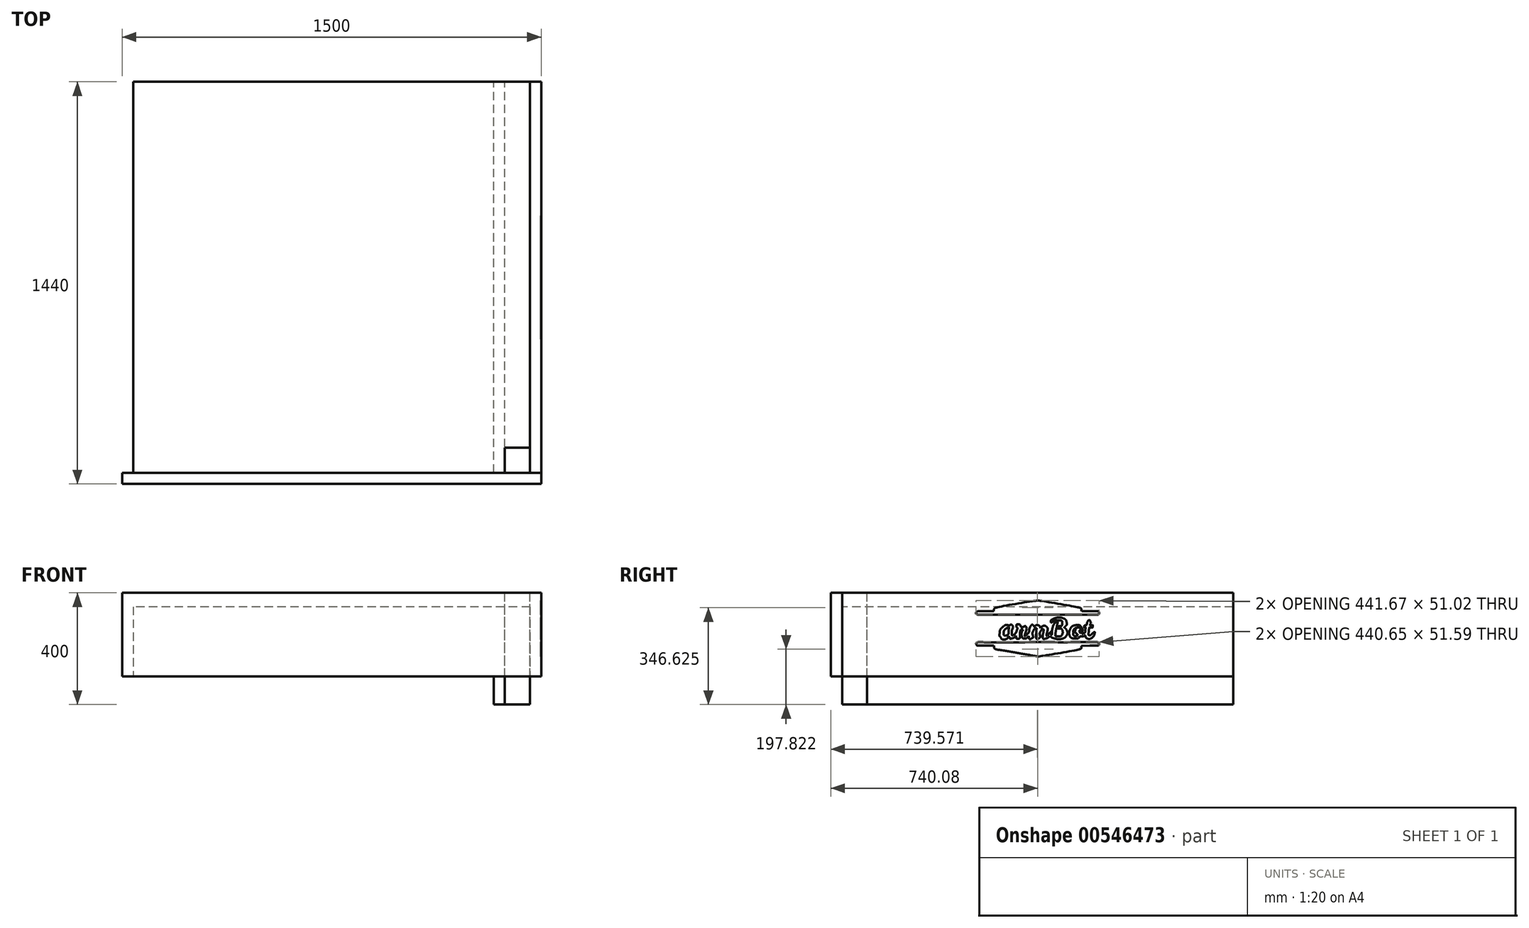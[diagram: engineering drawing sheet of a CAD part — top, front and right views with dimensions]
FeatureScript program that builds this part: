
annotation { "Feature Type Name" : "Feature", "Feature Type Description" : "" }
export const myFeature = defineFeature(function(context is Context, id is Id, definition is map)
    precondition{}
    {
        {
            var Q0;
            Q0=qCreatedBy(makeId("Top.planeOp"),FACE);
            var sketch = newSketch(context, id + "F0", { "sketchPlane" : qUnion([Q0])});
            skLineSegment(sketch, "E0.bottom", {"start": v(710, 700) * mm, "end": v(-710, 700) * mm});
            skLineSegment(sketch, "E0.top", {"start": v(710, -700) * mm, "end": v(-710, -700) * mm});
            skLineSegment(sketch, "E0.left", {"start": v(710, 700) * mm, "end": v(710, -700) * mm});
            skLineSegment(sketch, "E0.right", {"start": v(-710, 700) * mm, "end": v(-710, -700) * mm});
            skPoint(sketch, "E0.middle", {"position": v(0, 0) * mm});
            skSolve(sketch);
        }
        {
            var Q0;
            Q0=qSketchRegion(id+"F0",true);
            extrude(context, id + "F1", {"entities" : qUnion([Q0]), "depth" : 250 * mm});
        }
        {
            var Q0;
            Q0=makeQuery(id+"F1.opExtrude","SWEPT_FACE",FACE,{"disambiguationData":[OSD([sQuery(id+"F0.wireOp",EDGE,"E0.left")])]});
            var sketch = newSketch(context, id + "F2", { "sketchPlane" : qUnion([Q0])});
            skLineSegment(sketch, "E1.bottom", {"start": v(-700, 0) * mm, "end": v(700, 0) * mm});
            skLineSegment(sketch, "E1.top", {"start": v(-700, 300) * mm, "end": v(700, 300) * mm});
            skLineSegment(sketch, "E1.left", {"start": v(-700, 0) * mm, "end": v(-700, 300) * mm});
            skLineSegment(sketch, "E1.right", {"start": v(700, 0) * mm, "end": v(700, 300) * mm});
            skSolve(sketch);
        }
        {
            var Q0;
            Q0=qSketchRegion(id+"F2",true);
            extrude(context, id + "F3", {"entities" : qUnion([Q0]), "depth" : 40 * mm});
        }
        {
            var Q0;
            Q0=makeQuery(id+"F1.opExtrude","SWEPT_FACE",FACE,{"disambiguationData":[OSD([sQuery(id+"F0.wireOp",EDGE,"E0.top")])]});
            var sketch = newSketch(context, id + "F4", { "sketchPlane" : qUnion([Q0])});
            skLineSegment(sketch, "E2.bottom", {"start": v(-750, 300) * mm, "end": v(750, 300) * mm});
            skLineSegment(sketch, "E2.top", {"start": v(-750, 0) * mm, "end": v(750, 0) * mm});
            skLineSegment(sketch, "E2.left", {"start": v(-750, 300) * mm, "end": v(-750, 0) * mm});
            skLineSegment(sketch, "E2.right", {"start": v(750, 300) * mm, "end": v(750, 0) * mm});
            skSolve(sketch);
        }
        {
            var Q0;
            Q0=qSketchRegion(id+"F4",true);
            extrude(context, id + "F5", {"entities" : qUnion([Q0]), "depth" : 40 * mm});
        }
        {
            var Q0;
            Q0=makeQuery(id+"F1.opExtrude","CAP_FACE",FACE,{"disambiguationData":[OSD([sQuery(id+"F0.wireOp",EDGE,"E0.bottom"),sQuery(id+"F0.wireOp",EDGE,"E0.top"),sQuery(id+"F0.wireOp",EDGE,"E0.left"),sQuery(id+"F0.wireOp",EDGE,"E0.right")])],"isStart":false});
            var sketch = newSketch(context, id + "F6", { "sketchPlane" : qUnion([Q0])});
            skFitSpline(sketch, "E3", {"points": [v(-9.76, -247.93) * mm, v(-14.36, -247) * mm, v(-98.7, -232.48) * mm, v(-197.18, -215.67) * mm]});
            skFitSpline(sketch, "E4", {"points": [v(-197.18, -215.67) * mm, v(-303.5, -197.52) * mm, v(-377.79, -184.02) * mm, v(-380.05, -182.43) * mm]});
            skFitSpline(sketch, "E5", {"points": [v(-380.05, -182.43) * mm, v(-386.35, -178.01) * mm, v(-389.22, -172.54) * mm, v(-390.38, -162.7) * mm]});
            skLineSegment(sketch, "E6", {"start": v(-390.38, -162.7) * mm, "end": v(-391.49, -153.38) * mm});
            skLineSegment(sketch, "E7", {"start": v(-391.49, -153.38) * mm, "end": v(-463.29, -153.35) * mm});
            skFitSpline(sketch, "E8", {"points": [v(-463.29, -153.35) * mm, v(-540.74, -153.32) * mm, v(-542.21, -153.15) * mm, v(-546.84, -143.5) * mm]});
            skFitSpline(sketch, "E9", {"points": [v(-546.84, -143.5) * mm, v(-550.32, -136.23) * mm, v(-547.5, -129.03) * mm, v(-539.62, -125.02) * mm]});
            skFitSpline(sketch, "E10", {"points": [v(-539.62, -125.02) * mm, v(-533.58, -121.95) * mm, v(-503.94, -121.77) * mm, v(0.65, -121.77) * mm]});
            skFitSpline(sketch, "E11", {"points": [v(0.65, -121.77) * mm, v(385.66, -121.76) * mm, v(536.18, -122.34) * mm, v(540.43, -123.82) * mm]});
            skFitSpline(sketch, "E12", {"points": [v(540.43, -123.82) * mm, v(543.67, -124.95) * mm, v(547.14, -127.4) * mm, v(548.14, -129.27) * mm]});
            skFitSpline(sketch, "E13", {"points": [v(548.14, -129.27) * mm, v(551.05, -134.7) * mm, v(550.26, -143.3) * mm, v(546.41, -148.06) * mm]});
            skLineSegment(sketch, "E14", {"start": v(546.41, -148.06) * mm, "end": v(542.86, -152.45) * mm});
            skLineSegment(sketch, "E15", {"start": v(542.86, -152.45) * mm, "end": v(467.85, -153.38) * mm});
            skLineSegment(sketch, "E16", {"start": v(467.85, -153.38) * mm, "end": v(392.83, -154.3) * mm});
            skLineSegment(sketch, "E17", {"start": v(392.83, -154.3) * mm, "end": v(392.5, -162.05) * mm});
            skFitSpline(sketch, "E18", {"points": [v(392.5, -162.05) * mm, v(391.99, -173.78) * mm, v(387.68, -180.46) * mm, v(378.46, -183.85) * mm]});
            skFitSpline(sketch, "E19", {"points": [v(378.46, -183.85) * mm, v(371.97, -186.24) * mm, v(2.57, -250.58) * mm, v(-0.47, -249.85) * mm]});
            skFitSpline(sketch, "E20", {"points": [v(-0.47, -249.85) * mm, v(-0.98, -249.73) * mm, v(-5.16, -248.87) * mm, v(-9.76, -247.93) * mm]});
            skLineSegment(sketch, "E21", {"start": v(-9.76, -247.93) * mm, "end": v(-9.76, -247.93) * mm});
            skFitSpline(sketch, "E22", {"points": [v(163.18, -91.34) * mm, v(144.56, -86.99) * mm, v(127.82, -80.58) * mm, v(118.25, -74.15) * mm]});
            skLineSegment(sketch, "E23", {"start": v(118.25, -74.15) * mm, "end": v(108.82, -67.8) * mm});
            skLineSegment(sketch, "E24", {"start": v(108.82, -67.8) * mm, "end": v(101.7, -74.22) * mm});
            skFitSpline(sketch, "E25", {"points": [v(101.7, -74.22) * mm, v(92.92, -82.15) * mm, v(86.06, -85.78) * mm, v(75.22, -88.2) * mm]});
            skFitSpline(sketch, "E26", {"points": [v(75.22, -88.2) * mm, v(52.86, -93.22) * mm, v(44.33, -75.76) * mm, v(50.52, -37.64) * mm]});
            skFitSpline(sketch, "E27", {"points": [v(50.52, -37.64) * mm, v(54.63, -12.34) * mm, v(54.44, -8.7) * mm, v(48.9, -6.17) * mm]});
            skFitSpline(sketch, "E28", {"points": [v(48.9, -6.17) * mm, v(42.7, -3.35) * mm, v(36.64, -7.44) * mm, v(29.87, -18.99) * mm]});
            skFitSpline(sketch, "E29", {"points": [v(29.87, -18.99) * mm, v(21.01, -34.1) * mm, v(18.43, -44.15) * mm, v(20.53, -55.3) * mm]});
            skFitSpline(sketch, "E30", {"points": [v(20.53, -55.3) * mm, v(21.54, -60.66) * mm, v(22.46, -68.35) * mm, v(22.57, -72.38) * mm]});
            skFitSpline(sketch, "E31", {"points": [v(22.57, -72.38) * mm, v(22.76, -78.97) * mm, v(22, -80.26) * mm, v(14.95, -85.23) * mm]});
            skFitSpline(sketch, "E32", {"points": [v(14.95, -85.23) * mm, v(4.39, -92.68) * mm, v(-7.54, -93.24) * mm, v(-11.04, -86.43) * mm]});
            skFitSpline(sketch, "E33", {"points": [v(-11.04, -86.43) * mm, v(-13.95, -80.76) * mm, v(-14.16, -56.28) * mm, v(-11.54, -26.93) * mm]});
            skFitSpline(sketch, "E34", {"points": [v(-11.54, -26.93) * mm, v(-9.2, -0.66) * mm, v(-9.84, 2.83) * mm, v(-17.07, 2.83) * mm]});
            skFitSpline(sketch, "E35", {"points": [v(-17.07, 2.83) * mm, v(-23.9, 2.83) * mm, v(-30.46, -4.7) * mm, v(-38.87, -22.23) * mm]});
            skFitSpline(sketch, "E36", {"points": [v(-38.87, -22.23) * mm, v(-45.93, -36.93) * mm, v(-46.62, -45.33) * mm, v(-42.27, -63.77) * mm]});
            skFitSpline(sketch, "E37", {"points": [v(-42.27, -63.77) * mm, v(-38.91, -78.01) * mm, v(-39.9, -80.3) * mm, v(-52.19, -87) * mm]});
            skFitSpline(sketch, "E38", {"points": [v(-52.19, -87) * mm, v(-68.26, -95.75) * mm, v(-75.2, -92.86) * mm, v(-77.56, -76.43) * mm]});
            skLineSegment(sketch, "E39", {"start": v(-77.56, -76.43) * mm, "end": v(-78.86, -67.36) * mm});
            skLineSegment(sketch, "E40", {"start": v(-78.86, -67.36) * mm, "end": v(-86.62, -74.83) * mm});
            skFitSpline(sketch, "E41", {"points": [v(-86.62, -74.83) * mm, v(-97.05, -84.9) * mm, v(-104.92, -88.54) * mm, v(-116.78, -88.82) * mm]});
            skFitSpline(sketch, "E42", {"points": [v(-116.78, -88.82) * mm, v(-128.34, -89.1) * mm, v(-132.94, -86) * mm, v(-138.3, -74.35) * mm]});
            skFitSpline(sketch, "E43", {"points": [v(-138.3, -74.35) * mm, v(-144.12, -61.65) * mm, v(-141.58, -31.54) * mm, v(-133.32, -15.58) * mm]});
            skLineSegment(sketch, "E44", {"start": v(-133.32, -15.58) * mm, "end": v(-130.44, -10) * mm});
            skLineSegment(sketch, "E45", {"start": v(-130.44, -10) * mm, "end": v(-141.2, -10.56) * mm});
            skLineSegment(sketch, "E46", {"start": v(-141.2, -10.56) * mm, "end": v(-151.94, -11.12) * mm});
            skLineSegment(sketch, "E47", {"start": v(-151.94, -11.12) * mm, "end": v(-155.34, -25.07) * mm});
            skFitSpline(sketch, "E48", {"points": [v(-155.34, -25.07) * mm, v(-157.97, -35.9) * mm, v(-158.52, -43.56) * mm, v(-157.8, -59.34) * mm]});
            skFitSpline(sketch, "E49", {"points": [v(-157.8, -59.34) * mm, v(-157.29, -70.85) * mm, v(-157.67, -81.12) * mm, v(-158.7, -83.03) * mm]});
            skFitSpline(sketch, "E50", {"points": [v(-158.7, -83.03) * mm, v(-161.25, -87.81) * mm, v(-170.24, -92.01) * mm, v(-177.92, -92.01) * mm]});
            skFitSpline(sketch, "E51", {"points": [v(-177.92, -92.01) * mm, v(-186.08, -92.01) * mm, v(-189.42, -87.45) * mm, v(-191.2, -73.87) * mm]});
            skLineSegment(sketch, "E52", {"start": v(-191.2, -73.87) * mm, "end": v(-192.48, -64.09) * mm});
            skLineSegment(sketch, "E53", {"start": v(-192.48, -64.09) * mm, "end": v(-200.42, -71.4) * mm});
            skFitSpline(sketch, "E54", {"points": [v(-200.42, -71.4) * mm, v(-209.89, -80.13) * mm, v(-220.17, -85.65) * mm, v(-231.87, -88.27) * mm]});
            skFitSpline(sketch, "E55", {"points": [v(-231.87, -88.27) * mm, v(-243.7, -90.92) * mm, v(-250.08, -87.49) * mm, v(-254.4, -76.16) * mm]});
            skLineSegment(sketch, "E56", {"start": v(-254.4, -76.16) * mm, "end": v(-257.65, -67.68) * mm});
            skLineSegment(sketch, "E57", {"start": v(-257.65, -67.68) * mm, "end": v(-262.94, -74.1) * mm});
            skFitSpline(sketch, "E58", {"points": [v(-262.94, -74.1) * mm, v(-279.38, -94.04) * mm, v(-316.37, -95.84) * mm, v(-331.85, -77.45) * mm]});
            skFitSpline(sketch, "E59", {"points": [v(-331.85, -77.45) * mm, v(-339.17, -68.75) * mm, v(-341.42, -59.86) * mm, v(-340.14, -44.75) * mm]});
            skFitSpline(sketch, "E60", {"points": [v(-340.14, -44.75) * mm, v(-338.13, -20.94) * mm, v(-329.14, -1.86) * mm, v(-313.1, 12.61) * mm]});
            skFitSpline(sketch, "E61", {"points": [v(-313.1, 12.61) * mm, v(-297.94, 26.32) * mm, v(-276.95, 32.69) * mm, v(-259.7, 28.82) * mm]});
            skFitSpline(sketch, "E62", {"points": [v(-259.7, 28.82) * mm, v(-252.55, 27.22) * mm, v(-250.45, 27.38) * mm, v(-247.85, 29.73) * mm]});
            skFitSpline(sketch, "E63", {"points": [v(-247.85, 29.73) * mm, v(-240.93, 36) * mm, v(-226.99, 30.32) * mm, v(-220.73, 18.7) * mm]});
            skLineSegment(sketch, "E64", {"start": v(-220.73, 18.7) * mm, "end": v(-217.21, 12.17) * mm});
            skLineSegment(sketch, "E65", {"start": v(-217.21, 12.17) * mm, "end": v(-223.2, 0.02) * mm});
            skFitSpline(sketch, "E66", {"points": [v(-223.2, 0.02) * mm, v(-228.92, -11.58) * mm, v(-229.19, -13.1) * mm, v(-229.16, -33.94) * mm]});
            skFitSpline(sketch, "E67", {"points": [v(-229.16, -33.94) * mm, v(-229.13, -57.9) * mm, v(-228.1, -61.48) * mm, v(-221.81, -59.49) * mm]});
            skFitSpline(sketch, "E68", {"points": [v(-221.81, -59.49) * mm, v(-215.07, -57.35) * mm, v(-188.28, -30.28) * mm, v(-188.28, -25.6) * mm]});
            skFitSpline(sketch, "E69", {"points": [v(-188.28, -25.6) * mm, v(-188.28, -23.36) * mm, v(-186.22, -15.85) * mm, v(-183.7, -8.92) * mm]});
            skFitSpline(sketch, "E70", {"points": [v(-183.7, -8.92) * mm, v(-179.26, 3.33) * mm, v(-179.23, 3.78) * mm, v(-182.54, 7.44) * mm]});
            skFitSpline(sketch, "E71", {"points": [v(-182.54, 7.44) * mm, v(-188.48, 13.98) * mm, v(-190.53, 19.67) * mm, v(-189.3, 26.21) * mm]});
            skFitSpline(sketch, "E72", {"points": [v(-189.3, 26.21) * mm, v(-187.82, 34.15) * mm, v(-182.12, 38.16) * mm, v(-172.31, 38.16) * mm]});
            skFitSpline(sketch, "E73", {"points": [v(-172.31, 38.16) * mm, v(-163.16, 38.16) * mm, v(-156.23, 32.34) * mm, v(-150.73, 20.03) * mm]});
            skFitSpline(sketch, "E74", {"points": [v(-150.73, 20.03) * mm, v(-147.7, 13.24) * mm, v(-146.4, 12.12) * mm, v(-141.55, 12.12) * mm]});
            skFitSpline(sketch, "E75", {"points": [v(-141.55, 12.12) * mm, v(-138.45, 12.12) * mm, v(-130.4, 14.33) * mm, v(-123.66, 17.03) * mm]});
            skFitSpline(sketch, "E76", {"points": [v(-123.66, 17.03) * mm, v(-109.3, 22.78) * mm, v(-107.41, 22.17) * mm, v(-101.2, 9.8) * mm]});
            skLineSegment(sketch, "E77", {"start": v(-101.2, 9.8) * mm, "end": v(-96.87, 1.18) * mm});
            skLineSegment(sketch, "E78", {"start": v(-96.87, 1.18) * mm, "end": v(-104.6, -26.95) * mm});
            skFitSpline(sketch, "E79", {"points": [v(-104.6, -26.95) * mm, v(-115.26, -65.72) * mm, v(-113.52, -68.38) * mm, v(-91.12, -47.46) * mm]});
            skLineSegment(sketch, "E80", {"start": v(-91.12, -47.46) * mm, "end": v(-77.26, -34.51) * mm});
            skLineSegment(sketch, "E81", {"start": v(-77.26, -34.51) * mm, "end": v(-76.15, -22.7) * mm});
            skFitSpline(sketch, "E82", {"points": [v(-76.15, -22.7) * mm, v(-74.76, -7.77) * mm, v(-68.68, 10.87) * mm, v(-61.04, 23.61) * mm]});
            skFitSpline(sketch, "E83", {"points": [v(-61.04, 23.61) * mm, v(-56.21, 31.68) * mm, v(-54.07, 33.61) * mm, v(-49.45, 34.07) * mm]});
            skFitSpline(sketch, "E84", {"points": [v(-49.45, 34.07) * mm, v(-44.95, 34.52) * mm, v(-42.63, 33.32) * mm, v(-38.15, 28.2) * mm]});
            skFitSpline(sketch, "E85", {"points": [v(-38.15, 28.2) * mm, v(-35.04, 24.67) * mm, v(-32.16, 20.74) * mm, v(-31.73, 19.46) * mm]});
            skFitSpline(sketch, "E86", {"points": [v(-31.73, 19.46) * mm, v(-31.21, 17.9) * mm, v(-28.37, 19.02) * mm, v(-23, 22.9) * mm]});
            skFitSpline(sketch, "E87", {"points": [v(-23, 22.9) * mm, v(-11.96, 30.9) * mm, v(-1.17, 32.3) * mm, v(9.54, 27.1) * mm]});
            skFitSpline(sketch, "E88", {"points": [v(9.54, 27.1) * mm, v(18.23, 22.9) * mm, v(22.7, 17.7) * mm, v(24.79, 9.4) * mm]});
            skLineSegment(sketch, "E89", {"start": v(24.79, 9.4) * mm, "end": v(26.04, 4.44) * mm});
            skLineSegment(sketch, "E90", {"start": v(26.04, 4.44) * mm, "end": v(30.92, 9.1) * mm});
            skFitSpline(sketch, "E91", {"points": [v(30.92, 9.1) * mm, v(43.6, 21.22) * mm, v(66.06, 25.1) * mm, v(77.8, 17.18) * mm]});
            skFitSpline(sketch, "E92", {"points": [v(77.8, 17.18) * mm, v(81.26, 14.85) * mm, v(85.14, 10.88) * mm, v(86.42, 8.35) * mm]});
            skFitSpline(sketch, "E93", {"points": [v(86.42, 8.35) * mm, v(90.04, 1.18) * mm, v(89.21, -14.95) * mm, v(84.14, -35.88) * mm]});
            skFitSpline(sketch, "E94", {"points": [v(84.14, -35.88) * mm, v(81.59, -46.43) * mm, v(79.5, -56.26) * mm, v(79.5, -57.73) * mm]});
            skFitSpline(sketch, "E95", {"points": [v(79.5, -57.73) * mm, v(79.5, -63.6) * mm, v(86.26, -59.69) * mm, v(100.97, -45.33) * mm]});
            skFitSpline(sketch, "E96", {"points": [v(100.97, -45.33) * mm, v(110.63, -35.9) * mm, v(117.25, -30.77) * mm, v(118.65, -31.64) * mm]});
            skFitSpline(sketch, "E97", {"points": [v(118.65, -31.64) * mm, v(120.17, -32.58) * mm, v(120.56, -36.5) * mm, v(119.89, -43.92) * mm]});
            skFitSpline(sketch, "E98", {"points": [v(119.89, -43.92) * mm, v(118.95, -54.29) * mm, v(119.1, -54.82) * mm, v(123.1, -54.82) * mm]});
            skFitSpline(sketch, "E99", {"points": [v(123.1, -54.82) * mm, v(127.02, -54.82) * mm, v(127.36, -53.84) * mm, v(128.4, -39.48) * mm]});
            skFitSpline(sketch, "E100", {"points": [v(128.4, -39.48) * mm, v(130.72, -7.09) * mm, v(148.03, 43.77) * mm, v(160.6, 55.09) * mm]});
            skFitSpline(sketch, "E101", {"points": [v(160.6, 55.09) * mm, v(178.01, 70.78) * mm, v(179.9, 58.14) * mm, v(168.42, 2.83) * mm]});
            skFitSpline(sketch, "E102", {"points": [v(168.42, 2.83) * mm, v(163.73, -19.8) * mm, v(158.67, -63.5) * mm, v(160.5, -65.68) * mm]});
            skFitSpline(sketch, "E103", {"points": [v(160.5, -65.68) * mm, v(161.76, -67.18) * mm, v(175.96, -69.61) * mm, v(183.63, -69.64) * mm]});
            skFitSpline(sketch, "E104", {"points": [v(183.63, -69.64) * mm, v(200.98, -69.71) * mm, v(215.69, -61.64) * mm, v(220.83, -49.22) * mm]});
            skFitSpline(sketch, "E105", {"points": [v(220.83, -49.22) * mm, v(224.51, -40.34) * mm, v(222.43, -16.02) * mm, v(217.28, -7.68) * mm]});
            skFitSpline(sketch, "E106", {"points": [v(217.28, -7.68) * mm, v(213.13, -0.96) * mm, v(212.95, -0.9) * mm, v(200.63, -0.9) * mm]});
            skFitSpline(sketch, "E107", {"points": [v(200.63, -0.9) * mm, v(187.27, -0.9) * mm, v(181.1, 1.8) * mm, v(179.39, 8.35) * mm]});
            skFitSpline(sketch, "E108", {"points": [v(179.39, 8.35) * mm, v(178.82, 10.5) * mm, v(179.82, 13.89) * mm, v(181.7, 16.2) * mm]});
            skFitSpline(sketch, "E109", {"points": [v(181.7, 16.2) * mm, v(184.4, 19.56) * mm, v(187.56, 20.46) * mm, v(199.63, 21.31) * mm]});
            skFitSpline(sketch, "E110", {"points": [v(199.63, 21.31) * mm, v(213.63, 22.3) * mm, v(214.4, 22.6) * mm, v(217.02, 27.93) * mm]});
            skFitSpline(sketch, "E111", {"points": [v(217.02, 27.93) * mm, v(218.53, 31) * mm, v(219.77, 38.53) * mm, v(219.78, 44.67) * mm]});
            skFitSpline(sketch, "E112", {"points": [v(219.78, 44.67) * mm, v(219.8, 64.17) * mm, v(211.17, 71.67) * mm, v(187.07, 73.1) * mm]});
            skFitSpline(sketch, "E113", {"points": [v(187.07, 73.1) * mm, v(170.05, 74.11) * mm, v(157.7, 71.45) * mm, v(139.99, 62.97) * mm]});
            skFitSpline(sketch, "E114", {"points": [v(139.99, 62.97) * mm, v(124.82, 55.7) * mm, v(118.55, 54.98) * mm, v(118.55, 60.51) * mm]});
            skFitSpline(sketch, "E115", {"points": [v(118.55, 60.51) * mm, v(118.55, 70.5) * mm, v(143.11, 88.38) * mm, v(165.9, 94.95) * mm]});
            skFitSpline(sketch, "E116", {"points": [v(165.9, 94.95) * mm, v(181.16, 99.36) * mm, v(211.58, 97.92) * mm, v(227.33, 92.04) * mm]});
            skFitSpline(sketch, "E117", {"points": [v(227.33, 92.04) * mm, v(241.91, 86.6) * mm, v(254.67, 73.92) * mm, v(257.71, 61.83) * mm]});
            skFitSpline(sketch, "E118", {"points": [v(257.71, 61.83) * mm, v(262.48, 42.9) * mm, v(259.33, 31.38) * mm, v(245.79, 18.17) * mm]});
            skFitSpline(sketch, "E119", {"points": [v(245.79, 18.17) * mm, v(240.28, 12.8) * mm, v(236.48, 8.4) * mm, v(237.34, 8.4) * mm]});
            skFitSpline(sketch, "E120", {"points": [v(237.34, 8.4) * mm, v(241.01, 8.4) * mm, v(256.17, -7.19) * mm, v(259.81, -14.71) * mm]});
            skFitSpline(sketch, "E121", {"points": [v(259.81, -14.71) * mm, v(265.46, -26.39) * mm, v(265.68, -49.04) * mm, v(260.25, -59.68) * mm]});
            skFitSpline(sketch, "E122", {"points": [v(260.25, -59.68) * mm, v(254.38, -71.16) * mm, v(239.5, -83.55) * mm, v(225.92, -88.28) * mm]});
            skFitSpline(sketch, "E123", {"points": [v(225.92, -88.28) * mm, v(211.44, -93.33) * mm, v(178.53, -94.93) * mm, v(163.18, -91.34) * mm]});
            skFitSpline(sketch, "E124", {"points": [v(-281.84, -62.14) * mm, v(-267.85, -56.85) * mm, v(-259.05, -41.8) * mm, v(-258.98, -23.08) * mm]});
            skFitSpline(sketch, "E125", {"points": [v(-258.98, -23.08) * mm, v(-258.96, -16.37) * mm, v(-258.05, -6.04) * mm, v(-256.95, -0.12) * mm]});
            skFitSpline(sketch, "E126", {"points": [v(-256.95, -0.12) * mm, v(-255.86, 5.8) * mm, v(-255.42, 11.09) * mm, v(-255.98, 11.64) * mm]});
            skFitSpline(sketch, "E127", {"points": [v(-255.98, 11.64) * mm, v(-257.93, 13.6) * mm, v(-273.99, 6.15) * mm, v(-282.7, -0.75) * mm]});
            skFitSpline(sketch, "E128", {"points": [v(-282.7, -0.75) * mm, v(-295.24, -10.66) * mm, v(-302.1, -24.16) * mm, v(-303.18, -41.06) * mm]});
            skFitSpline(sketch, "E129", {"points": [v(-303.18, -41.06) * mm, v(-303.98, -53.62) * mm, v(-303.72, -54.84) * mm, v(-299.24, -59.32) * mm]});
            skFitSpline(sketch, "E130", {"points": [v(-299.24, -59.32) * mm, v(-294.03, -64.53) * mm, v(-289.93, -65.2) * mm, v(-281.84, -62.14) * mm]});
            skFitSpline(sketch, "E131", {"points": [v(-459.3, -89.94) * mm, v(-464.48, -84.62) * mm, v(-460.7, -35.47) * mm, v(-453.32, -12.23) * mm]});
            skFitSpline(sketch, "E132", {"points": [v(-453.32, -12.23) * mm, v(-452.15, -8.52) * mm, v(-452.73, -8.33) * mm, v(-465.23, -8.33) * mm]});
            skFitSpline(sketch, "E133", {"points": [v(-465.23, -8.33) * mm, v(-476.68, -8.33) * mm, v(-478.37, -7.9) * mm, v(-478.37, -4.96) * mm]});
            skFitSpline(sketch, "E134", {"points": [v(-478.37, -4.96) * mm, v(-478.37, 0.26) * mm, v(-468.99, 8.03) * mm, v(-457.1, 12.63) * mm]});
            skLineSegment(sketch, "E135", {"start": v(-457.1, 12.63) * mm, "end": v(-446.32, 16.8) * mm});
            skLineSegment(sketch, "E136", {"start": v(-446.32, 16.8) * mm, "end": v(-438.43, 39.1) * mm});
            skFitSpline(sketch, "E137", {"points": [v(-438.43, 39.1) * mm, v(-434.08, 51.37) * mm, v(-429.87, 62.96) * mm, v(-429.07, 64.87) * mm]});
            skFitSpline(sketch, "E138", {"points": [v(-429.07, 64.87) * mm, v(-427.72, 68.05) * mm, v(-428.28, 68.22) * mm, v(-435.78, 67) * mm]});
            skFitSpline(sketch, "E139", {"points": [v(-435.78, 67) * mm, v(-447.95, 65.04) * mm, v(-458.5, 59.86) * mm, v(-467.75, 51.34) * mm]});
            skFitSpline(sketch, "E140", {"points": [v(-467.75, 51.34) * mm, v(-479.66, 40.36) * mm, v(-483.95, 41.51) * mm, v(-483.95, 55.7) * mm]});
            skFitSpline(sketch, "E141", {"points": [v(-483.95, 55.7) * mm, v(-483.95, 68.83) * mm, v(-467.73, 83.32) * mm, v(-445.28, 90.26) * mm]});
            skFitSpline(sketch, "E142", {"points": [v(-445.28, 90.26) * mm, v(-427.1, 95.87) * mm, v(-406.05, 97.33) * mm, v(-358.74, 96.25) * mm]});
            skFitSpline(sketch, "E143", {"points": [v(-358.74, 96.25) * mm, v(-311.18, 95.17) * mm, v(-311.95, 95.43) * mm, v(-317.58, 82.22) * mm]});
            skFitSpline(sketch, "E144", {"points": [v(-317.58, 82.22) * mm, v(-323.64, 68.03) * mm, v(-324, 67.91) * mm, v(-360.96, 67.88) * mm]});
            skLineSegment(sketch, "E145", {"start": v(-360.96, 67.88) * mm, "end": v(-393.76, 67.85) * mm});
            skLineSegment(sketch, "E146", {"start": v(-393.76, 67.85) * mm, "end": v(-398.66, 47.9) * mm});
            skFitSpline(sketch, "E147", {"points": [v(-398.66, 47.9) * mm, v(-401.36, 36.91) * mm, v(-403.87, 26.67) * mm, v(-404.24, 25.14) * mm]});
            skFitSpline(sketch, "E148", {"points": [v(-404.24, 25.14) * mm, v(-404.8, 22.8) * mm, v(-401.23, 22.27) * mm, v(-381.74, 21.83) * mm]});
            skFitSpline(sketch, "E149", {"points": [v(-381.74, 21.83) * mm, v(-367.15, 21.5) * mm, v(-358.1, 20.53) * mm, v(-357.28, 19.21) * mm]});
            skFitSpline(sketch, "E150", {"points": [v(-357.28, 19.21) * mm, v(-355.76, 16.75) * mm, v(-359.89, 2.02) * mm, v(-363.24, -2.01) * mm]});
            skFitSpline(sketch, "E151", {"points": [v(-363.24, -2.01) * mm, v(-365.2, -4.38) * mm, v(-369.3, -4.62) * mm, v(-389.06, -3.54) * mm]});
            skLineSegment(sketch, "E152", {"start": v(-389.06, -3.54) * mm, "end": v(-412.56, -2.27) * mm});
            skLineSegment(sketch, "E153", {"start": v(-412.56, -2.27) * mm, "end": v(-416.52, -18.78) * mm});
            skFitSpline(sketch, "E154", {"points": [v(-416.52, -18.78) * mm, v(-421.04, -37.64) * mm, v(-423.77, -53.93) * mm, v(-425.45, -72.08) * mm]});
            skFitSpline(sketch, "E155", {"points": [v(-425.45, -72.08) * mm, v(-426.44, -82.86) * mm, v(-427.3, -85.14) * mm, v(-431.33, -87.78) * mm]});
            skFitSpline(sketch, "E156", {"points": [v(-431.33, -87.78) * mm, v(-437.41, -91.77) * mm, v(-456.13, -93.2) * mm, v(-459.3, -89.94) * mm]});
            skFitSpline(sketch, "E157", {"points": [v(317.5, -88.5) * mm, v(302.9, -83.79) * mm, v(289.51, -71.3) * mm, v(285.81, -58.96) * mm]});
            skFitSpline(sketch, "E158", {"points": [v(285.81, -58.96) * mm, v(282.17, -46.8) * mm, v(284.25, -22.14) * mm, v(289.96, -9.87) * mm]});
            skFitSpline(sketch, "E159", {"points": [v(289.96, -9.87) * mm, v(299.26, 10.12) * mm, v(316.09, 24.32) * mm, v(335.9, 28.9) * mm]});
            skFitSpline(sketch, "E160", {"points": [v(335.9, 28.9) * mm, v(354.07, 33.1) * mm, v(378.44, 28.13) * mm, v(386.33, 18.63) * mm]});
            skFitSpline(sketch, "E161", {"points": [v(386.33, 18.63) * mm, v(390.02, 14.18) * mm, v(386.8, 12.82) * mm, v(369.86, 11.65) * mm]});
            skFitSpline(sketch, "E162", {"points": [v(369.86, 11.65) * mm, v(362, 11.12) * mm, v(352.6, 9.43) * mm, v(348.96, 7.91) * mm]});
            skFitSpline(sketch, "E163", {"points": [v(348.96, 7.91) * mm, v(331.95, 0.8) * mm, v(320.77, -16.17) * mm, v(320.52, -35.3) * mm]});
            skFitSpline(sketch, "E164", {"points": [v(320.52, -35.3) * mm, v(320.22, -57.93) * mm, v(334.52, -68.41) * mm, v(357.15, -62.13) * mm]});
            skLineSegment(sketch, "E165", {"start": v(357.15, -62.13) * mm, "end": v(364.23, -60.16) * mm});
            skLineSegment(sketch, "E166", {"start": v(364.23, -60.16) * mm, "end": v(357.84, -53.09) * mm});
            skFitSpline(sketch, "E167", {"points": [v(357.84, -53.09) * mm, v(336.45, -29.41) * mm, v(349.03, 6.55) * mm, v(378.7, 6.55) * mm]});
            skFitSpline(sketch, "E168", {"points": [v(378.7, 6.55) * mm, v(389.23, 6.55) * mm, v(395.06, 3.8) * mm, v(399.43, -3.17) * mm]});
            skFitSpline(sketch, "E169", {"points": [v(399.43, -3.17) * mm, v(402.65, -8.3) * mm, v(403.12, -11.47) * mm, v(402.44, -23.2) * mm]});
            skFitSpline(sketch, "E170", {"points": [v(402.44, -23.2) * mm, v(402, -30.88) * mm, v(401.02, -39.04) * mm, v(400.27, -41.34) * mm]});
            skFitSpline(sketch, "E171", {"points": [v(400.27, -41.34) * mm, v(398.58, -46.51) * mm, v(402.33, -46.92) * mm, v(411.06, -42.52) * mm]});
            skFitSpline(sketch, "E172", {"points": [v(411.06, -42.52) * mm, v(421.31, -37.33) * mm, v(425.37, -32.45) * mm, v(425.44, -25.2) * mm]});
            skFitSpline(sketch, "E173", {"points": [v(425.44, -25.2) * mm, v(425.48, -21.55) * mm, v(426.6, -12.92) * mm, v(427.94, -6.02) * mm]});
            skFitSpline(sketch, "E174", {"points": [v(427.94, -6.02) * mm, v(429.27, 0.87) * mm, v(429.94, 6.94) * mm, v(429.42, 7.46) * mm]});
            skFitSpline(sketch, "E175", {"points": [v(429.42, 7.46) * mm, v(428.9, 7.98) * mm, v(425.6, 8.4) * mm, v(422.07, 8.4) * mm]});
            skFitSpline(sketch, "E176", {"points": [v(422.07, 8.4) * mm, v(415.71, 8.4) * mm, v(415.67, 8.46) * mm, v(416.93, 15.14) * mm]});
            skFitSpline(sketch, "E177", {"points": [v(416.93, 15.14) * mm, v(418.93, 25.81) * mm, v(421.68, 28.86) * mm, v(429.3, 28.86) * mm]});
            skFitSpline(sketch, "E178", {"points": [v(429.3, 28.86) * mm, v(435.8, 28.86) * mm, v(436.17, 29.23) * mm, v(439.97, 39.55) * mm]});
            skFitSpline(sketch, "E179", {"points": [v(439.97, 39.55) * mm, v(450.84, 69.05) * mm, v(465.01, 75.94) * mm, v(473.83, 56) * mm]});
            skLineSegment(sketch, "E180", {"start": v(473.83, 56) * mm, "end": v(477.45, 47.84) * mm});
            skLineSegment(sketch, "E181", {"start": v(477.45, 47.84) * mm, "end": v(472.82, 39.75) * mm});
            skFitSpline(sketch, "E182", {"points": [v(472.82, 39.75) * mm, v(470.27, 35.3) * mm, v(468.18, 31.02) * mm, v(468.17, 30.25) * mm]});
            skFitSpline(sketch, "E183", {"points": [v(468.17, 30.25) * mm, v(468.15, 29.49) * mm, v(474, 28.86) * mm, v(481.16, 28.86) * mm]});
            skFitSpline(sketch, "E184", {"points": [v(481.16, 28.86) * mm, v(493.59, 28.86) * mm, v(494.18, 28.66) * mm, v(494.18, 24.49) * mm]});
            skFitSpline(sketch, "E185", {"points": [v(494.18, 24.49) * mm, v(494.18, 22.08) * mm, v(493.26, 17.48) * mm, v(492.14, 14.26) * mm]});
            skFitSpline(sketch, "E186", {"points": [v(492.14, 14.26) * mm, v(490.1, 8.41) * mm, v(490.07, 8.4) * mm, v(476.53, 8.4) * mm]});
            skFitSpline(sketch, "E187", {"points": [v(476.53, 8.4) * mm, v(466.58, 8.4) * mm, v(462.7, 7.7) * mm, v(461.96, 5.79) * mm]});
            skFitSpline(sketch, "E188", {"points": [v(461.96, 5.79) * mm, v(461.4, 4.35) * mm, v(459.93, -6.74) * mm, v(458.69, -18.85) * mm]});
            skFitSpline(sketch, "E189", {"points": [v(458.69, -18.85) * mm, v(456.19, -43.13) * mm, v(457.42, -58.1) * mm, v(462.05, -59.89) * mm]});
            skFitSpline(sketch, "E190", {"points": [v(462.05, -59.89) * mm, v(466.54, -61.6) * mm, v(480.7, -53.25) * mm, v(493.44, -41.34) * mm]});
            skFitSpline(sketch, "E191", {"points": [v(493.44, -41.34) * mm, v(499.73, -35.46) * mm, v(505.73, -30.65) * mm, v(506.77, -30.65) * mm]});
            skFitSpline(sketch, "E192", {"points": [v(506.77, -30.65) * mm, v(510.1, -30.65) * mm, v(511.02, -39.58) * mm, v(508.46, -47.01) * mm]});
            skFitSpline(sketch, "E193", {"points": [v(508.46, -47.01) * mm, v(500.27, -70.78) * mm, v(464.23, -93.67) * mm, v(443.63, -88.18) * mm]});
            skFitSpline(sketch, "E194", {"points": [v(443.63, -88.18) * mm, v(436.32, -86.23) * mm, v(430.49, -78.96) * mm, v(428.05, -68.77) * mm]});
            skFitSpline(sketch, "E195", {"points": [v(428.05, -68.77) * mm, v(426, -60.18) * mm, v(425.55, -59.99) * mm, v(418.25, -64.52) * mm]});
            skFitSpline(sketch, "E196", {"points": [v(418.25, -64.52) * mm, v(412.67, -68) * mm, v(408.97, -68.73) * mm, v(397.88, -68.57) * mm]});
            skFitSpline(sketch, "E197", {"points": [v(397.88, -68.57) * mm, v(384.98, -68.4) * mm, v(384.01, -68.68) * mm, v(377.5, -74.64) * mm]});
            skFitSpline(sketch, "E198", {"points": [v(377.5, -74.64) * mm, v(365.8, -85.37) * mm, v(355.8, -89.15) * mm, v(337.98, -89.6) * mm]});
            skFitSpline(sketch, "E199", {"points": [v(337.98, -89.6) * mm, v(329.28, -89.82) * mm, v(320.07, -89.33) * mm, v(317.5, -88.5) * mm]});
            skFitSpline(sketch, "E200", {"points": [v(385.7, -25.43) * mm, v(386.64, -17.46) * mm, v(386.3, -15.64) * mm, v(383.66, -14.63) * mm]});
            skFitSpline(sketch, "E201", {"points": [v(383.66, -14.63) * mm, v(379.08, -12.87) * mm, v(376.38, -16.52) * mm, v(376.67, -24.09) * mm]});
            skFitSpline(sketch, "E202", {"points": [v(376.67, -24.09) * mm, v(376.97, -32.15) * mm, v(380.4, -39.18) * mm, v(382.83, -36.75) * mm]});
            skFitSpline(sketch, "E203", {"points": [v(382.83, -36.75) * mm, v(383.78, -35.8) * mm, v(385.07, -30.7) * mm, v(385.7, -25.43) * mm]});
            skFitSpline(sketch, "E204", {"points": [v(-539.73, 126.1) * mm, v(-551.06, 131.84) * mm, v(-551, 146.27) * mm, v(-539.62, 152.05) * mm]});
            skFitSpline(sketch, "E205", {"points": [v(-539.62, 152.05) * mm, v(-533.86, 154.98) * mm, v(-526.13, 155.3) * mm, v(-462.1, 155.3) * mm]});
            skLineSegment(sketch, "E206", {"start": v(-462.1, 155.3) * mm, "end": v(-390.97, 155.3) * mm});
            skLineSegment(sketch, "E207", {"start": v(-390.97, 155.3) * mm, "end": v(-390.97, 160.85) * mm});
            skFitSpline(sketch, "E208", {"points": [v(-390.97, 160.85) * mm, v(-390.97, 170.05) * mm, v(-385.48, 181.2) * mm, v(-379.4, 184.35) * mm]});
            skFitSpline(sketch, "E209", {"points": [v(-379.4, 184.35) * mm, v(-373.17, 187.57) * mm, v(-10.28, 250.15) * mm, v(2.18, 250.15) * mm]});
            skFitSpline(sketch, "E210", {"points": [v(2.18, 250.15) * mm, v(10.33, 250.15) * mm, v(362.94, 190.41) * mm, v(375.5, 186.9) * mm]});
            skFitSpline(sketch, "E211", {"points": [v(375.5, 186.9) * mm, v(384.93, 184.27) * mm, v(391.52, 175.86) * mm, v(393.02, 164.53) * mm]});
            skLineSegment(sketch, "E212", {"start": v(393.02, 164.53) * mm, "end": v(394.24, 155.3) * mm});
            skLineSegment(sketch, "E213", {"start": v(394.24, 155.3) * mm, "end": v(464.39, 155.3) * mm});
            skFitSpline(sketch, "E214", {"points": [v(464.39, 155.3) * mm, v(536.67, 155.3) * mm, v(544.5, 154.6) * mm, v(548.14, 147.8) * mm]});
            skFitSpline(sketch, "E215", {"points": [v(548.14, 147.8) * mm, v(551.05, 142.36) * mm, v(550.26, 133.77) * mm, v(546.41, 129.02) * mm]});
            skLineSegment(sketch, "E216", {"start": v(546.41, 129.02) * mm, "end": v(542.86, 124.63) * mm});
            skLineSegment(sketch, "E217", {"start": v(542.86, 124.63) * mm, "end": v(3.88, 124.18) * mm});
            skFitSpline(sketch, "E218", {"points": [v(3.88, 124.18) * mm, v(-428.24, 123.83) * mm, v(-536, 124.2) * mm, v(-539.73, 126.1) * mm]});
            skLineSegment(sketch, "E219", {"start": v(-539.73, 126.1) * mm, "end": v(-539.73, 126.1) * mm});
            skSolve(sketch);
        }
        {
            var Q0;
            Q0=makeQuery(id+"F3.opExtrude","CAP_FACE",FACE,{"disambiguationData":[OSD([sQuery(id+"F2.wireOp",EDGE,"E1.bottom"),sQuery(id+"F2.wireOp",EDGE,"E1.top"),sQuery(id+"F2.wireOp",EDGE,"E1.left"),sQuery(id+"F2.wireOp",EDGE,"E1.right")])],"isStart":false});
            var sketch = newSketch(context, id + "F7", { "sketchPlane" : qUnion([Q0])});
            skFitSpline(sketch, "E220", {"points": [v(-4.02, 72.8) * mm, v(-5.86, 73.18) * mm, v(-39.6, 78.99) * mm, v(-78.98, 85.71) * mm]});
            skFitSpline(sketch, "E221", {"points": [v(-78.98, 85.71) * mm, v(-121.51, 92.97) * mm, v(-151.23, 98.37) * mm, v(-152.13, 99) * mm]});
            skFitSpline(sketch, "E222", {"points": [v(-152.13, 99) * mm, v(-154.65, 100.77) * mm, v(-155.8, 102.96) * mm, v(-156.27, 106.9) * mm]});
            skLineSegment(sketch, "E223", {"start": v(-156.27, 106.9) * mm, "end": v(-156.7, 110.63) * mm});
            skLineSegment(sketch, "E224", {"start": v(-156.7, 110.63) * mm, "end": v(-185.43, 110.64) * mm});
            skFitSpline(sketch, "E225", {"points": [v(-185.43, 110.64) * mm, v(-216.4, 110.65) * mm, v(-217, 110.72) * mm, v(-218.85, 114.58) * mm]});
            skFitSpline(sketch, "E226", {"points": [v(-218.85, 114.58) * mm, v(-220.24, 117.49) * mm, v(-219.12, 120.37) * mm, v(-215.96, 121.97) * mm]});
            skFitSpline(sketch, "E227", {"points": [v(-215.96, 121.97) * mm, v(-213.54, 123.2) * mm, v(-201.69, 123.27) * mm, v(0.15, 123.27) * mm]});
            skFitSpline(sketch, "E228", {"points": [v(0.15, 123.27) * mm, v(154.15, 123.27) * mm, v(214.36, 123.04) * mm, v(216.06, 122.45) * mm]});
            skFitSpline(sketch, "E229", {"points": [v(216.06, 122.45) * mm, v(217.36, 122) * mm, v(218.75, 121.02) * mm, v(219.15, 120.27) * mm]});
            skFitSpline(sketch, "E230", {"points": [v(219.15, 120.27) * mm, v(220.3, 118.1) * mm, v(220, 114.66) * mm, v(218.45, 112.76) * mm]});
            skLineSegment(sketch, "E231", {"start": v(218.45, 112.76) * mm, "end": v(217.03, 111) * mm});
            skLineSegment(sketch, "E232", {"start": v(217.03, 111) * mm, "end": v(187.03, 110.63) * mm});
            skLineSegment(sketch, "E233", {"start": v(187.03, 110.63) * mm, "end": v(157.02, 110.26) * mm});
            skLineSegment(sketch, "E234", {"start": v(157.02, 110.26) * mm, "end": v(156.89, 107.16) * mm});
            skFitSpline(sketch, "E235", {"points": [v(156.89, 107.16) * mm, v(156.68, 102.47) * mm, v(154.96, 99.8) * mm, v(151.27, 98.44) * mm]});
            skFitSpline(sketch, "E236", {"points": [v(151.27, 98.44) * mm, v(148.68, 97.48) * mm, v(0.92, 71.75) * mm, v(-0.3, 72.04) * mm]});
            skFitSpline(sketch, "E237", {"points": [v(-0.3, 72.04) * mm, v(-0.5, 72.09) * mm, v(-2.18, 72.43) * mm, v(-4.02, 72.8) * mm]});
            skLineSegment(sketch, "E238", {"start": v(-4.02, 72.8) * mm, "end": v(-4.02, 72.8) * mm});
            skFitSpline(sketch, "E239", {"points": [v(65.16, 135.44) * mm, v(57.71, 137.18) * mm, v(51.02, 139.75) * mm, v(47.2, 142.32) * mm]});
            skLineSegment(sketch, "E240", {"start": v(47.2, 142.32) * mm, "end": v(43.41, 144.86) * mm});
            skLineSegment(sketch, "E241", {"start": v(43.41, 144.86) * mm, "end": v(40.57, 142.3) * mm});
            skFitSpline(sketch, "E242", {"points": [v(40.57, 142.3) * mm, v(37.06, 139.12) * mm, v(34.31, 137.67) * mm, v(29.98, 136.7) * mm]});
            skFitSpline(sketch, "E243", {"points": [v(29.98, 136.7) * mm, v(21.03, 134.7) * mm, v(17.62, 141.67) * mm, v(20.1, 156.92) * mm]});
            skFitSpline(sketch, "E244", {"points": [v(20.1, 156.92) * mm, v(21.74, 167.04) * mm, v(21.67, 168.5) * mm, v(19.44, 169.51) * mm]});
            skFitSpline(sketch, "E245", {"points": [v(19.44, 169.51) * mm, v(16.97, 170.64) * mm, v(14.54, 169) * mm, v(11.84, 164.39) * mm]});
            skFitSpline(sketch, "E246", {"points": [v(11.84, 164.39) * mm, v(8.3, 158.34) * mm, v(7.26, 154.32) * mm, v(8.1, 149.86) * mm]});
            skFitSpline(sketch, "E247", {"points": [v(8.1, 149.86) * mm, v(8.5, 147.71) * mm, v(8.87, 144.64) * mm, v(8.92, 143.03) * mm]});
            skFitSpline(sketch, "E248", {"points": [v(8.92, 143.03) * mm, v(9, 140.4) * mm, v(8.69, 139.88) * mm, v(5.87, 137.89) * mm]});
            skFitSpline(sketch, "E249", {"points": [v(5.87, 137.89) * mm, v(1.64, 134.9) * mm, v(-3.13, 134.68) * mm, v(-4.53, 137.4) * mm]});
            skFitSpline(sketch, "E250", {"points": [v(-4.53, 137.4) * mm, v(-5.7, 139.68) * mm, v(-5.78, 149.47) * mm, v(-4.73, 161.2) * mm]});
            skFitSpline(sketch, "E251", {"points": [v(-4.73, 161.2) * mm, v(-3.79, 171.71) * mm, v(-4.05, 173.1) * mm, v(-6.94, 173.1) * mm]});
            skFitSpline(sketch, "E252", {"points": [v(-6.94, 173.1) * mm, v(-9.67, 173.1) * mm, v(-12.3, 170.1) * mm, v(-15.66, 163.09) * mm]});
            skFitSpline(sketch, "E253", {"points": [v(-15.66, 163.09) * mm, v(-18.48, 157.2) * mm, v(-18.76, 153.85) * mm, v(-17.02, 146.47) * mm]});
            skFitSpline(sketch, "E254", {"points": [v(-17.02, 146.47) * mm, v(-15.68, 140.78) * mm, v(-16.07, 139.86) * mm, v(-20.99, 137.18) * mm]});
            skFitSpline(sketch, "E255", {"points": [v(-20.99, 137.18) * mm, v(-27.42, 133.68) * mm, v(-30.19, 134.83) * mm, v(-31.13, 141.4) * mm]});
            skLineSegment(sketch, "E256", {"start": v(-31.13, 141.4) * mm, "end": v(-31.66, 145.04) * mm});
            skLineSegment(sketch, "E257", {"start": v(-31.66, 145.04) * mm, "end": v(-34.76, 142.05) * mm});
            skFitSpline(sketch, "E258", {"points": [v(-34.76, 142.05) * mm, v(-38.93, 138.02) * mm, v(-42.08, 136.56) * mm, v(-46.82, 136.45) * mm]});
            skFitSpline(sketch, "E259", {"points": [v(-46.82, 136.45) * mm, v(-51.45, 136.34) * mm, v(-53.29, 137.58) * mm, v(-55.43, 142.24) * mm]});
            skFitSpline(sketch, "E260", {"points": [v(-55.43, 142.24) * mm, v(-57.76, 147.32) * mm, v(-56.74, 159.36) * mm, v(-53.44, 165.75) * mm]});
            skLineSegment(sketch, "E261", {"start": v(-53.44, 165.75) * mm, "end": v(-52.29, 167.98) * mm});
            skLineSegment(sketch, "E262", {"start": v(-52.29, 167.98) * mm, "end": v(-56.59, 167.76) * mm});
            skLineSegment(sketch, "E263", {"start": v(-56.59, 167.76) * mm, "end": v(-60.89, 167.53) * mm});
            skLineSegment(sketch, "E264", {"start": v(-60.89, 167.53) * mm, "end": v(-62.25, 161.95) * mm});
            skFitSpline(sketch, "E265", {"points": [v(-62.25, 161.95) * mm, v(-63.3, 157.62) * mm, v(-63.52, 154.56) * mm, v(-63.24, 148.25) * mm]});
            skFitSpline(sketch, "E266", {"points": [v(-63.24, 148.25) * mm, v(-63.03, 143.64) * mm, v(-63.18, 139.53) * mm, v(-63.59, 138.77) * mm]});
            skFitSpline(sketch, "E267", {"points": [v(-63.59, 138.77) * mm, v(-64.61, 136.85) * mm, v(-68.2, 135.17) * mm, v(-71.28, 135.17) * mm]});
            skFitSpline(sketch, "E268", {"points": [v(-71.28, 135.17) * mm, v(-74.54, 135.17) * mm, v(-75.88, 137) * mm, v(-76.6, 142.43) * mm]});
            skLineSegment(sketch, "E269", {"start": v(-76.6, 142.43) * mm, "end": v(-77.1, 146.34) * mm});
            skLineSegment(sketch, "E270", {"start": v(-77.1, 146.34) * mm, "end": v(-80.28, 143.42) * mm});
            skFitSpline(sketch, "E271", {"points": [v(-80.28, 143.42) * mm, v(-84.07, 139.93) * mm, v(-88.18, 137.72) * mm, v(-92.86, 136.67) * mm]});
            skFitSpline(sketch, "E272", {"points": [v(-92.86, 136.67) * mm, v(-97.59, 135.61) * mm, v(-100.15, 136.99) * mm, v(-101.87, 141.51) * mm]});
            skLineSegment(sketch, "E273", {"start": v(-101.87, 141.51) * mm, "end": v(-103.17, 144.9) * mm});
            skLineSegment(sketch, "E274", {"start": v(-103.17, 144.9) * mm, "end": v(-105.29, 142.34) * mm});
            skFitSpline(sketch, "E275", {"points": [v(-105.29, 142.34) * mm, v(-111.87, 134.36) * mm, v(-126.66, 133.64) * mm, v(-132.85, 141) * mm]});
            skFitSpline(sketch, "E276", {"points": [v(-132.85, 141) * mm, v(-135.78, 144.48) * mm, v(-136.68, 148.03) * mm, v(-136.17, 154.08) * mm]});
            skFitSpline(sketch, "E277", {"points": [v(-136.17, 154.08) * mm, v(-135.36, 163.6) * mm, v(-131.77, 171.23) * mm, v(-125.36, 177.03) * mm]});
            skFitSpline(sketch, "E278", {"points": [v(-125.36, 177.03) * mm, v(-119.29, 182.5) * mm, v(-110.9, 185.05) * mm, v(-104, 183.5) * mm]});
            skFitSpline(sketch, "E279", {"points": [v(-104, 183.5) * mm, v(-101.13, 182.87) * mm, v(-100.3, 182.93) * mm, v(-99.25, 183.87) * mm]});
            skFitSpline(sketch, "E280", {"points": [v(-99.25, 183.87) * mm, v(-96.48, 186.38) * mm, v(-90.9, 184.1) * mm, v(-88.4, 179.46) * mm]});
            skLineSegment(sketch, "E281", {"start": v(-88.4, 179.46) * mm, "end": v(-87, 176.85) * mm});
            skLineSegment(sketch, "E282", {"start": v(-87, 176.85) * mm, "end": v(-89.4, 171.99) * mm});
            skFitSpline(sketch, "E283", {"points": [v(-89.4, 171.99) * mm, v(-91.68, 167.35) * mm, v(-91.79, 166.74) * mm, v(-91.78, 158.4) * mm]});
            skFitSpline(sketch, "E284", {"points": [v(-91.78, 158.4) * mm, v(-91.76, 148.82) * mm, v(-91.35, 147.39) * mm, v(-88.84, 148.18) * mm]});
            skFitSpline(sketch, "E285", {"points": [v(-88.84, 148.18) * mm, v(-86.14, 149.04) * mm, v(-75.42, 159.87) * mm, v(-75.42, 161.74) * mm]});
            skFitSpline(sketch, "E286", {"points": [v(-75.42, 161.74) * mm, v(-75.42, 162.64) * mm, v(-74.6, 165.64) * mm, v(-73.6, 168.41) * mm]});
            skFitSpline(sketch, "E287", {"points": [v(-73.6, 168.41) * mm, v(-71.82, 173.31) * mm, v(-71.8, 173.5) * mm, v(-73.13, 174.95) * mm]});
            skFitSpline(sketch, "E288", {"points": [v(-73.13, 174.95) * mm, v(-75.5, 177.57) * mm, v(-76.32, 179.85) * mm, v(-75.83, 182.46) * mm]});
            skFitSpline(sketch, "E289", {"points": [v(-75.83, 182.46) * mm, v(-75.24, 185.64) * mm, v(-72.96, 187.24) * mm, v(-69.04, 187.24) * mm]});
            skFitSpline(sketch, "E290", {"points": [v(-69.04, 187.24) * mm, v(-65.37, 187.24) * mm, v(-62.6, 184.92) * mm, v(-60.4, 180) * mm]});
            skFitSpline(sketch, "E291", {"points": [v(-60.4, 180) * mm, v(-59.19, 177.28) * mm, v(-58.67, 176.83) * mm, v(-56.73, 176.83) * mm]});
            skFitSpline(sketch, "E292", {"points": [v(-56.73, 176.83) * mm, v(-55.5, 176.83) * mm, v(-52.27, 177.71) * mm, v(-49.58, 178.8) * mm]});
            skFitSpline(sketch, "E293", {"points": [v(-49.58, 178.8) * mm, v(-43.83, 181.09) * mm, v(-43.08, 180.85) * mm, v(-40.6, 175.9) * mm]});
            skLineSegment(sketch, "E294", {"start": v(-40.6, 175.9) * mm, "end": v(-38.86, 172.45) * mm});
            skLineSegment(sketch, "E295", {"start": v(-38.86, 172.45) * mm, "end": v(-41.95, 161.2) * mm});
            skFitSpline(sketch, "E296", {"points": [v(-41.95, 161.2) * mm, v(-46.22, 145.7) * mm, v(-45.52, 144.63) * mm, v(-36.56, 153) * mm]});
            skLineSegment(sketch, "E297", {"start": v(-36.56, 153) * mm, "end": v(-31.01, 158.17) * mm});
            skLineSegment(sketch, "E298", {"start": v(-31.01, 158.17) * mm, "end": v(-30.57, 162.9) * mm});
            skFitSpline(sketch, "E299", {"points": [v(-30.57, 162.9) * mm, v(-30.02, 168.87) * mm, v(-27.58, 176.33) * mm, v(-24.53, 181.43) * mm]});
            skFitSpline(sketch, "E300", {"points": [v(-24.53, 181.43) * mm, v(-22.6, 184.65) * mm, v(-21.74, 185.42) * mm, v(-19.9, 185.6) * mm]});
            skFitSpline(sketch, "E301", {"points": [v(-19.9, 185.6) * mm, v(-18.1, 185.79) * mm, v(-17.17, 185.3) * mm, v(-15.37, 183.26) * mm]});
            skFitSpline(sketch, "E302", {"points": [v(-15.37, 183.26) * mm, v(-14.13, 181.85) * mm, v(-12.97, 180.27) * mm, v(-12.8, 179.76) * mm]});
            skFitSpline(sketch, "E303", {"points": [v(-12.8, 179.76) * mm, v(-12.6, 179.14) * mm, v(-11.46, 179.59) * mm, v(-9.31, 181.14) * mm]});
            skFitSpline(sketch, "E304", {"points": [v(-9.31, 181.14) * mm, v(-4.9, 184.34) * mm, v(-0.58, 184.9) * mm, v(3.7, 182.82) * mm]});
            skFitSpline(sketch, "E305", {"points": [v(3.7, 182.82) * mm, v(7.18, 181.14) * mm, v(8.97, 179.06) * mm, v(9.8, 175.74) * mm]});
            skLineSegment(sketch, "E306", {"start": v(9.8, 175.74) * mm, "end": v(10.3, 173.75) * mm});
            skLineSegment(sketch, "E307", {"start": v(10.3, 173.75) * mm, "end": v(12.25, 175.62) * mm});
            skFitSpline(sketch, "E308", {"points": [v(12.25, 175.62) * mm, v(17.33, 180.47) * mm, v(26.31, 182.02) * mm, v(31, 178.85) * mm]});
            skFitSpline(sketch, "E309", {"points": [v(31, 178.85) * mm, v(32.4, 177.92) * mm, v(33.94, 176.33) * mm, v(34.45, 175.32) * mm]});
            skFitSpline(sketch, "E310", {"points": [v(34.45, 175.32) * mm, v(35.9, 172.45) * mm, v(35.57, 166) * mm, v(33.55, 157.63) * mm]});
            skFitSpline(sketch, "E311", {"points": [v(33.55, 157.63) * mm, v(32.52, 153.4) * mm, v(31.69, 149.48) * mm, v(31.69, 148.89) * mm]});
            skFitSpline(sketch, "E312", {"points": [v(31.69, 148.89) * mm, v(31.69, 146.54) * mm, v(34.4, 148.1) * mm, v(40.28, 153.85) * mm]});
            skFitSpline(sketch, "E313", {"points": [v(40.28, 153.85) * mm, v(44.14, 157.62) * mm, v(46.79, 159.67) * mm, v(47.35, 159.33) * mm]});
            skFitSpline(sketch, "E314", {"points": [v(47.35, 159.33) * mm, v(47.95, 158.95) * mm, v(48.11, 157.38) * mm, v(47.84, 154.41) * mm]});
            skFitSpline(sketch, "E315", {"points": [v(47.84, 154.41) * mm, v(47.47, 150.27) * mm, v(47.53, 150.05) * mm, v(49.13, 150.05) * mm]});
            skFitSpline(sketch, "E316", {"points": [v(49.13, 150.05) * mm, v(50.7, 150.05) * mm, v(50.83, 150.44) * mm, v(51.25, 156.19) * mm]});
            skFitSpline(sketch, "E317", {"points": [v(51.25, 156.19) * mm, v(52.17, 169.14) * mm, v(59.1, 189.49) * mm, v(64.13, 194.01) * mm]});
            skFitSpline(sketch, "E318", {"points": [v(64.13, 194.01) * mm, v(71.1, 200.3) * mm, v(71.85, 195.23) * mm, v(67.26, 173.1) * mm]});
            skFitSpline(sketch, "E319", {"points": [v(67.26, 173.1) * mm, v(65.38, 164.06) * mm, v(63.36, 146.58) * mm, v(64.09, 145.7) * mm]});
            skFitSpline(sketch, "E320", {"points": [v(64.09, 145.7) * mm, v(64.6, 145.1) * mm, v(70.27, 144.14) * mm, v(73.34, 144.12) * mm]});
            skFitSpline(sketch, "E321", {"points": [v(73.34, 144.12) * mm, v(80.28, 144.1) * mm, v(86.16, 147.32) * mm, v(88.22, 152.3) * mm]});
            skFitSpline(sketch, "E322", {"points": [v(88.22, 152.3) * mm, v(89.7, 155.84) * mm, v(88.86, 165.57) * mm, v(86.8, 168.9) * mm]});
            skFitSpline(sketch, "E323", {"points": [v(86.8, 168.9) * mm, v(85.14, 171.6) * mm, v(85.07, 171.62) * mm, v(80.14, 171.62) * mm]});
            skFitSpline(sketch, "E324", {"points": [v(80.14, 171.62) * mm, v(74.8, 171.62) * mm, v(72.33, 172.7) * mm, v(71.64, 175.32) * mm]});
            skFitSpline(sketch, "E325", {"points": [v(71.64, 175.32) * mm, v(71.42, 176.18) * mm, v(71.81, 177.53) * mm, v(72.57, 178.46) * mm]});
            skFitSpline(sketch, "E326", {"points": [v(72.57, 178.46) * mm, v(73.65, 179.8) * mm, v(74.91, 180.16) * mm, v(79.74, 180.5) * mm]});
            skFitSpline(sketch, "E327", {"points": [v(79.74, 180.5) * mm, v(85.34, 180.9) * mm, v(85.65, 181.02) * mm, v(86.7, 183.15) * mm]});
            skFitSpline(sketch, "E328", {"points": [v(86.7, 183.15) * mm, v(87.3, 184.38) * mm, v(87.8, 187.4) * mm, v(87.8, 189.85) * mm]});
            skFitSpline(sketch, "E329", {"points": [v(87.8, 189.85) * mm, v(87.81, 197.65) * mm, v(84.36, 200.65) * mm, v(74.71, 201.22) * mm]});
            skFitSpline(sketch, "E330", {"points": [v(74.71, 201.22) * mm, v(67.9, 201.62) * mm, v(62.96, 200.56) * mm, v(55.88, 197.17) * mm]});
            skFitSpline(sketch, "E331", {"points": [v(55.88, 197.17) * mm, v(49.82, 194.26) * mm, v(47.3, 193.97) * mm, v(47.3, 196.18) * mm]});
            skFitSpline(sketch, "E332", {"points": [v(47.3, 196.18) * mm, v(47.3, 200.18) * mm, v(57.13, 207.33) * mm, v(66.24, 209.96) * mm]});
            skFitSpline(sketch, "E333", {"points": [v(66.24, 209.96) * mm, v(72.35, 211.72) * mm, v(84.52, 211.15) * mm, v(90.82, 208.8) * mm]});
            skFitSpline(sketch, "E334", {"points": [v(90.82, 208.8) * mm, v(96.65, 206.62) * mm, v(101.76, 201.55) * mm, v(102.97, 196.71) * mm]});
            skFitSpline(sketch, "E335", {"points": [v(102.97, 196.71) * mm, v(104.88, 189.14) * mm, v(103.62, 184.53) * mm, v(98.2, 179.25) * mm]});
            skFitSpline(sketch, "E336", {"points": [v(98.2, 179.25) * mm, v(96, 177.1) * mm, v(94.48, 175.34) * mm, v(94.82, 175.34) * mm]});
            skFitSpline(sketch, "E337", {"points": [v(94.82, 175.34) * mm, v(96.3, 175.34) * mm, v(102.36, 169.1) * mm, v(103.81, 166.1) * mm]});
            skFitSpline(sketch, "E338", {"points": [v(103.81, 166.1) * mm, v(106.07, 161.42) * mm, v(106.16, 152.36) * mm, v(103.99, 148.1) * mm]});
            skFitSpline(sketch, "E339", {"points": [v(103.99, 148.1) * mm, v(101.64, 143.52) * mm, v(95.7, 138.56) * mm, v(90.26, 136.67) * mm]});
            skFitSpline(sketch, "E340", {"points": [v(90.26, 136.67) * mm, v(84.46, 134.65) * mm, v(71.3, 134) * mm, v(65.16, 135.44) * mm]});
            skFitSpline(sketch, "E341", {"points": [v(-112.85, 147.12) * mm, v(-107.25, 149.24) * mm, v(-103.73, 155.26) * mm, v(-103.7, 162.75) * mm]});
            skFitSpline(sketch, "E342", {"points": [v(-103.7, 162.75) * mm, v(-103.7, 165.43) * mm, v(-103.33, 169.57) * mm, v(-102.9, 171.93) * mm]});
            skFitSpline(sketch, "E343", {"points": [v(-102.9, 171.93) * mm, v(-102.46, 174.3) * mm, v(-102.28, 176.41) * mm, v(-102.5, 176.64) * mm]});
            skFitSpline(sketch, "E344", {"points": [v(-102.5, 176.64) * mm, v(-103.28, 177.42) * mm, v(-109.7, 174.44) * mm, v(-113.2, 171.68) * mm]});
            skFitSpline(sketch, "E345", {"points": [v(-113.2, 171.68) * mm, v(-118.2, 167.72) * mm, v(-120.95, 162.32) * mm, v(-121.38, 155.55) * mm]});
            skFitSpline(sketch, "E346", {"points": [v(-121.38, 155.55) * mm, v(-121.7, 150.53) * mm, v(-121.6, 150.04) * mm, v(-119.8, 148.25) * mm]});
            skFitSpline(sketch, "E347", {"points": [v(-119.8, 148.25) * mm, v(-117.72, 146.17) * mm, v(-116.09, 145.9) * mm, v(-112.85, 147.12) * mm]});
            skFitSpline(sketch, "E348", {"points": [v(-183.84, 136) * mm, v(-185.9, 138.13) * mm, v(-184.4, 157.8) * mm, v(-181.44, 167.09) * mm]});
            skFitSpline(sketch, "E349", {"points": [v(-181.44, 167.09) * mm, v(-180.97, 168.57) * mm, v(-181.2, 168.65) * mm, v(-186.2, 168.65) * mm]});
            skFitSpline(sketch, "E350", {"points": [v(-186.2, 168.65) * mm, v(-190.78, 168.65) * mm, v(-191.46, 168.82) * mm, v(-191.46, 170) * mm]});
            skFitSpline(sketch, "E351", {"points": [v(-191.46, 170) * mm, v(-191.46, 172.08) * mm, v(-187.7, 175.19) * mm, v(-182.96, 177.03) * mm]});
            skLineSegment(sketch, "E352", {"start": v(-182.96, 177.03) * mm, "end": v(-178.64, 178.7) * mm});
            skLineSegment(sketch, "E353", {"start": v(-178.64, 178.7) * mm, "end": v(-175.48, 187.62) * mm});
            skFitSpline(sketch, "E354", {"points": [v(-175.48, 187.62) * mm, v(-173.75, 192.53) * mm, v(-172.06, 197.16) * mm, v(-171.74, 197.93) * mm]});
            skFitSpline(sketch, "E355", {"points": [v(-171.74, 197.93) * mm, v(-171.2, 199.2) * mm, v(-171.42, 199.27) * mm, v(-174.43, 198.78) * mm]});
            skFitSpline(sketch, "E356", {"points": [v(-174.43, 198.78) * mm, v(-179.3, 198) * mm, v(-183.51, 195.92) * mm, v(-187.21, 192.52) * mm]});
            skFitSpline(sketch, "E357", {"points": [v(-187.21, 192.52) * mm, v(-191.98, 188.12) * mm, v(-193.7, 188.58) * mm, v(-193.7, 194.26) * mm]});
            skFitSpline(sketch, "E358", {"points": [v(-193.7, 194.26) * mm, v(-193.7, 199.51) * mm, v(-187.2, 205.3) * mm, v(-178.22, 208.08) * mm]});
            skFitSpline(sketch, "E359", {"points": [v(-178.22, 208.08) * mm, v(-170.95, 210.33) * mm, v(-162.53, 210.91) * mm, v(-143.6, 210.48) * mm]});
            skFitSpline(sketch, "E360", {"points": [v(-143.6, 210.48) * mm, v(-124.58, 210.05) * mm, v(-124.9, 210.15) * mm, v(-127.15, 204.87) * mm]});
            skFitSpline(sketch, "E361", {"points": [v(-127.15, 204.87) * mm, v(-129.57, 199.2) * mm, v(-129.71, 199.15) * mm, v(-144.5, 199.13) * mm]});
            skLineSegment(sketch, "E362", {"start": v(-144.5, 199.13) * mm, "end": v(-157.62, 199.12) * mm});
            skLineSegment(sketch, "E363", {"start": v(-157.62, 199.12) * mm, "end": v(-159.58, 191.14) * mm});
            skFitSpline(sketch, "E364", {"points": [v(-159.58, 191.14) * mm, v(-160.65, 186.74) * mm, v(-161.66, 182.65) * mm, v(-161.8, 182.04) * mm]});
            skFitSpline(sketch, "E365", {"points": [v(-161.8, 182.04) * mm, v(-162.04, 181.1) * mm, v(-160.6, 180.89) * mm, v(-152.8, 180.7) * mm]});
            skFitSpline(sketch, "E366", {"points": [v(-152.8, 180.7) * mm, v(-146.97, 180.58) * mm, v(-143.35, 180.2) * mm, v(-143.02, 179.66) * mm]});
            skFitSpline(sketch, "E367", {"points": [v(-143.02, 179.66) * mm, v(-142.41, 178.68) * mm, v(-144.07, 172.79) * mm, v(-145.4, 171.17) * mm]});
            skFitSpline(sketch, "E368", {"points": [v(-145.4, 171.17) * mm, v(-146.2, 170.23) * mm, v(-147.83, 170.13) * mm, v(-155.74, 170.56) * mm]});
            skLineSegment(sketch, "E369", {"start": v(-155.74, 170.56) * mm, "end": v(-165.13, 171.07) * mm});
            skLineSegment(sketch, "E370", {"start": v(-165.13, 171.07) * mm, "end": v(-166.72, 164.47) * mm});
            skFitSpline(sketch, "E371", {"points": [v(-166.72, 164.47) * mm, v(-168.53, 156.92) * mm, v(-169.62, 150.4) * mm, v(-170.3, 143.15) * mm]});
            skFitSpline(sketch, "E372", {"points": [v(-170.3, 143.15) * mm, v(-170.69, 138.84) * mm, v(-171.03, 137.92) * mm, v(-172.64, 136.87) * mm]});
            skFitSpline(sketch, "E373", {"points": [v(-172.64, 136.87) * mm, v(-175.08, 135.27) * mm, v(-182.56, 134.7) * mm, v(-183.84, 136) * mm]});
            skFitSpline(sketch, "E374", {"points": [v(126.9, 136.58) * mm, v(121.05, 138.46) * mm, v(115.7, 143.46) * mm, v(114.21, 148.4) * mm]});
            skFitSpline(sketch, "E375", {"points": [v(114.21, 148.4) * mm, v(112.76, 153.26) * mm, v(113.59, 163.12) * mm, v(115.87, 168.03) * mm]});
            skFitSpline(sketch, "E376", {"points": [v(115.87, 168.03) * mm, v(119.6, 176.03) * mm, v(126.32, 181.7) * mm, v(134.25, 183.54) * mm]});
            skFitSpline(sketch, "E377", {"points": [v(134.25, 183.54) * mm, v(141.52, 185.22) * mm, v(151.26, 183.23) * mm, v(154.42, 179.43) * mm]});
            skFitSpline(sketch, "E378", {"points": [v(154.42, 179.43) * mm, v(155.9, 177.65) * mm, v(154.6, 177.1) * mm, v(147.83, 176.64) * mm]});
            skFitSpline(sketch, "E379", {"points": [v(147.83, 176.64) * mm, v(144.69, 176.43) * mm, v(140.93, 175.75) * mm, v(139.47, 175.14) * mm]});
            skFitSpline(sketch, "E380", {"points": [v(139.47, 175.14) * mm, v(132.67, 172.3) * mm, v(128.2, 165.5) * mm, v(128.1, 157.86) * mm]});
            skFitSpline(sketch, "E381", {"points": [v(128.1, 157.86) * mm, v(127.97, 148.8) * mm, v(133.7, 144.61) * mm, v(142.75, 147.13) * mm]});
            skLineSegment(sketch, "E382", {"start": v(142.75, 147.13) * mm, "end": v(145.58, 147.91) * mm});
            skLineSegment(sketch, "E383", {"start": v(145.58, 147.91) * mm, "end": v(143.02, 150.75) * mm});
            skFitSpline(sketch, "E384", {"points": [v(143.02, 150.75) * mm, v(134.47, 160.22) * mm, v(139.5, 174.6) * mm, v(151.37, 174.6) * mm]});
            skFitSpline(sketch, "E385", {"points": [v(151.37, 174.6) * mm, v(155.58, 174.6) * mm, v(157.91, 173.5) * mm, v(159.66, 170.71) * mm]});
            skFitSpline(sketch, "E386", {"points": [v(159.66, 170.71) * mm, v(160.95, 168.66) * mm, v(161.14, 167.4) * mm, v(160.87, 162.7) * mm]});
            skFitSpline(sketch, "E387", {"points": [v(160.87, 162.7) * mm, v(160.69, 159.63) * mm, v(160.3, 156.36) * mm, v(160, 155.44) * mm]});
            skFitSpline(sketch, "E388", {"points": [v(160, 155.44) * mm, v(159.32, 153.37) * mm, v(160.82, 153.21) * mm, v(164.31, 154.97) * mm]});
            skFitSpline(sketch, "E389", {"points": [v(164.31, 154.97) * mm, v(168.41, 157.05) * mm, v(170.04, 159) * mm, v(170.07, 161.9) * mm]});
            skFitSpline(sketch, "E390", {"points": [v(170.07, 161.9) * mm, v(170.08, 163.36) * mm, v(170.53, 166.81) * mm, v(171.06, 169.57) * mm]});
            skFitSpline(sketch, "E391", {"points": [v(171.06, 169.57) * mm, v(171.6, 172.33) * mm, v(171.86, 174.76) * mm, v(171.66, 174.96) * mm]});
            skFitSpline(sketch, "E392", {"points": [v(171.66, 174.96) * mm, v(171.45, 175.17) * mm, v(170.12, 175.34) * mm, v(168.72, 175.34) * mm]});
            skFitSpline(sketch, "E393", {"points": [v(168.72, 175.34) * mm, v(166.17, 175.34) * mm, v(166.16, 175.36) * mm, v(166.66, 178.04) * mm]});
            skFitSpline(sketch, "E394", {"points": [v(166.66, 178.04) * mm, v(167.46, 182.3) * mm, v(168.56, 183.52) * mm, v(171.6, 183.52) * mm]});
            skFitSpline(sketch, "E395", {"points": [v(171.6, 183.52) * mm, v(174.2, 183.52) * mm, v(174.36, 183.67) * mm, v(175.88, 187.8) * mm]});
            skFitSpline(sketch, "E396", {"points": [v(175.88, 187.8) * mm, v(180.22, 199.6) * mm, v(185.9, 202.36) * mm, v(189.42, 194.38) * mm]});
            skLineSegment(sketch, "E397", {"start": v(189.42, 194.38) * mm, "end": v(190.87, 191.12) * mm});
            skLineSegment(sketch, "E398", {"start": v(190.87, 191.12) * mm, "end": v(189.02, 187.88) * mm});
            skFitSpline(sketch, "E399", {"points": [v(189.02, 187.88) * mm, v(188, 186.1) * mm, v(187.16, 184.39) * mm, v(187.15, 184.08) * mm]});
            skFitSpline(sketch, "E400", {"points": [v(187.15, 184.08) * mm, v(187.15, 183.77) * mm, v(189.49, 183.52) * mm, v(192.35, 183.52) * mm]});
            skFitSpline(sketch, "E401", {"points": [v(192.35, 183.52) * mm, v(197.32, 183.52) * mm, v(197.56, 183.44) * mm, v(197.56, 181.77) * mm]});
            skFitSpline(sketch, "E402", {"points": [v(197.56, 181.77) * mm, v(197.56, 180.81) * mm, v(197.2, 178.97) * mm, v(196.74, 177.68) * mm]});
            skFitSpline(sketch, "E403", {"points": [v(196.74, 177.68) * mm, v(195.93, 175.35) * mm, v(195.92, 175.34) * mm, v(190.5, 175.34) * mm]});
            skFitSpline(sketch, "E404", {"points": [v(190.5, 175.34) * mm, v(186.52, 175.34) * mm, v(184.97, 175.06) * mm, v(184.67, 174.3) * mm]});
            skFitSpline(sketch, "E405", {"points": [v(184.67, 174.3) * mm, v(184.45, 173.72) * mm, v(183.86, 169.28) * mm, v(183.36, 164.44) * mm]});
            skFitSpline(sketch, "E406", {"points": [v(183.36, 164.44) * mm, v(182.36, 154.73) * mm, v(182.85, 148.74) * mm, v(184.7, 148.02) * mm]});
            skFitSpline(sketch, "E407", {"points": [v(184.7, 148.02) * mm, v(186.5, 147.34) * mm, v(192.17, 150.68) * mm, v(197.26, 155.44) * mm]});
            skFitSpline(sketch, "E408", {"points": [v(197.26, 155.44) * mm, v(199.78, 157.8) * mm, v(202.18, 159.72) * mm, v(202.6, 159.72) * mm]});
            skFitSpline(sketch, "E409", {"points": [v(202.6, 159.72) * mm, v(203.93, 159.72) * mm, v(204.3, 156.15) * mm, v(203.27, 153.17) * mm]});
            skFitSpline(sketch, "E410", {"points": [v(203.27, 153.17) * mm, v(200, 143.67) * mm, v(185.58, 134.51) * mm, v(177.34, 136.7) * mm]});
            skFitSpline(sketch, "E411", {"points": [v(177.34, 136.7) * mm, v(174.42, 137.49) * mm, v(172.08, 140.4) * mm, v(171.1, 144.47) * mm]});
            skFitSpline(sketch, "E412", {"points": [v(171.1, 144.47) * mm, v(170.29, 147.9) * mm, v(170.1, 147.99) * mm, v(167.19, 146.17) * mm]});
            skFitSpline(sketch, "E413", {"points": [v(167.19, 146.17) * mm, v(164.96, 144.78) * mm, v(163.48, 144.49) * mm, v(159.04, 144.55) * mm]});
            skFitSpline(sketch, "E414", {"points": [v(159.04, 144.55) * mm, v(153.88, 144.62) * mm, v(153.5, 144.5) * mm, v(150.9, 142.12) * mm]});
            skFitSpline(sketch, "E415", {"points": [v(150.9, 142.12) * mm, v(146.2, 137.83) * mm, v(142.2, 136.32) * mm, v(135.08, 136.14) * mm]});
            skFitSpline(sketch, "E416", {"points": [v(135.08, 136.14) * mm, v(131.6, 136.05) * mm, v(127.92, 136.25) * mm, v(126.9, 136.58) * mm]});
            skFitSpline(sketch, "E417", {"points": [v(154.17, 161.8) * mm, v(154.55, 165) * mm, v(154.4, 165.72) * mm, v(153.35, 166.13) * mm]});
            skFitSpline(sketch, "E418", {"points": [v(153.35, 166.13) * mm, v(151.52, 166.83) * mm, v(150.44, 165.37) * mm, v(150.55, 162.34) * mm]});
            skFitSpline(sketch, "E419", {"points": [v(150.55, 162.34) * mm, v(150.68, 159.12) * mm, v(152.04, 156.3) * mm, v(153.02, 157.28) * mm]});
            skFitSpline(sketch, "E420", {"points": [v(153.02, 157.28) * mm, v(153.4, 157.66) * mm, v(153.92, 159.7) * mm, v(154.17, 161.8) * mm]});
            skFitSpline(sketch, "E421", {"points": [v(-216, 222.42) * mm, v(-220.54, 224.72) * mm, v(-220.51, 230.49) * mm, v(-215.96, 232.8) * mm]});
            skFitSpline(sketch, "E422", {"points": [v(-215.96, 232.8) * mm, v(-213.66, 233.97) * mm, v(-210.56, 234.1) * mm, v(-184.95, 234.1) * mm]});
            skLineSegment(sketch, "E423", {"start": v(-184.95, 234.1) * mm, "end": v(-156.5, 234.1) * mm});
            skLineSegment(sketch, "E424", {"start": v(-156.5, 234.1) * mm, "end": v(-156.5, 236.32) * mm});
            skFitSpline(sketch, "E425", {"points": [v(-156.5, 236.32) * mm, v(-156.5, 240) * mm, v(-154.3, 244.46) * mm, v(-151.87, 245.72) * mm]});
            skFitSpline(sketch, "E426", {"points": [v(-151.87, 245.72) * mm, v(-149.38, 247) * mm, v(-4.22, 272.04) * mm, v(0.76, 272.04) * mm]});
            skFitSpline(sketch, "E427", {"points": [v(0.76, 272.04) * mm, v(4.02, 272.04) * mm, v(145.06, 248.14) * mm, v(150.09, 246.74) * mm]});
            skFitSpline(sketch, "E428", {"points": [v(150.09, 246.74) * mm, v(153.86, 245.69) * mm, v(156.5, 242.32) * mm, v(157.1, 237.8) * mm]});
            skLineSegment(sketch, "E429", {"start": v(157.1, 237.8) * mm, "end": v(157.58, 234.1) * mm});
            skLineSegment(sketch, "E430", {"start": v(157.58, 234.1) * mm, "end": v(185.64, 234.1) * mm});
            skFitSpline(sketch, "E431", {"points": [v(185.64, 234.1) * mm, v(214.56, 234.1) * mm, v(217.69, 233.82) * mm, v(219.15, 231.1) * mm]});
            skFitSpline(sketch, "E432", {"points": [v(219.15, 231.1) * mm, v(220.3, 228.93) * mm, v(220, 225.49) * mm, v(218.45, 223.59) * mm]});
            skLineSegment(sketch, "E433", {"start": v(218.45, 223.59) * mm, "end": v(217.03, 221.83) * mm});
            skLineSegment(sketch, "E434", {"start": v(217.03, 221.83) * mm, "end": v(1.44, 221.65) * mm});
            skFitSpline(sketch, "E435", {"points": [v(1.44, 221.65) * mm, v(-171.4, 221.51) * mm, v(-214.51, 221.66) * mm, v(-216, 222.42) * mm]});
            skLineSegment(sketch, "E436", {"start": v(-216, -140.24) * mm, "end": v(-216, -140.24) * mm});
            skSolve(sketch);
        }
        {
            var Q0;
            Q0=qSketchRegion(id+"F7",true);
            extrude(context, id + "F8", {"entities" : qUnion([Q0]), "operationType" : NewBodyOperationType.REMOVE, "oppositeDirection" : true, "depth" : 2 * mm});
        }
        {
            var Q0;
            Q0=makeQuery(id+"F3.opExtrude","SWEPT_FACE",FACE,{"disambiguationData":[OSD([sQuery(id+"F2.wireOp",EDGE,"E1.top")])]});
            var sketch = newSketch(context, id + "F9", { "sketchPlane" : qUnion([Q0])});
            skLineSegment(sketch, "E437.bottom", {"start": v(710, -700) * mm, "end": v(620, -700) * mm});
            skLineSegment(sketch, "E437.top", {"start": v(710, -610) * mm, "end": v(620, -610) * mm});
            skLineSegment(sketch, "E437.left", {"start": v(710, -700) * mm, "end": v(710, -610) * mm});
            skLineSegment(sketch, "E437.right", {"start": v(620, -700) * mm, "end": v(620, -610) * mm});
            skSolve(sketch);
        }
        {
            var Q0;
            Q0=makeQuery(id+"F9.imprint","IMPRINT",FACE,{"disambiguationData":[TD([[makeQuery(id+"F9.imprint","IMPRINT",EDGE,{"derivedFrom":sQuery(id+"F9.wireOp",EDGE,"E437.bottom")}),-1.0]])]});
            extrude(context, id + "F10", {"entities" : qUnion([Q0]), "oppositeDirection" : true, "depth" : 400 * mm});
        }
        {
            var Q0;
            Q0=makeQuery(id+"F10.opExtrude","SWEPT_FACE",FACE,{"disambiguationData":[OSD([sQuery(id+"F9.wireOp",EDGE,"E437.right")])]});
            var sketch = newSketch(context, id + "F11", { "sketchPlane" : qUnion([Q0])});
            skLineSegment(sketch, "E438.bottom", {"start": v(700, -100) * mm, "end": v(-700, -100) * mm});
            skLineSegment(sketch, "E438.top", {"start": v(700, 0) * mm, "end": v(-700, 0) * mm});
            skLineSegment(sketch, "E438.left", {"start": v(700, -100) * mm, "end": v(700, 0) * mm});
            skLineSegment(sketch, "E438.right", {"start": v(-700, -100) * mm, "end": v(-700, 0) * mm});
            skSolve(sketch);
        }
        {
            var Q0;
            {var subQ3=sQuery(id+"F11.wireOp",EDGE,"E438.right");Q0=makeQuery(id+"F11.imprint","IMPRINT",FACE,{"disambiguationData":[TD([[makeQuery(id+"F11.imprint","IMPRINT",EDGE,{"derivedFrom":subQ3}),-1.0]])]});}
            var Q1;
            {var subQ0=sQuery(id+"F11.wireOp",EDGE,"E438.left");Q1=makeQuery(id+"F11.imprint","IMPRINT",FACE,{"disambiguationData":[TD([[makeQuery(id+"F11.imprint","IMPRINT",EDGE,{"derivedFrom":subQ0}),1.0]])]});}
            extrude(context, id + "F12", {"entities" : qUnion([Q0, Q1]), "depth" : 40 * mm});
        }
    });
